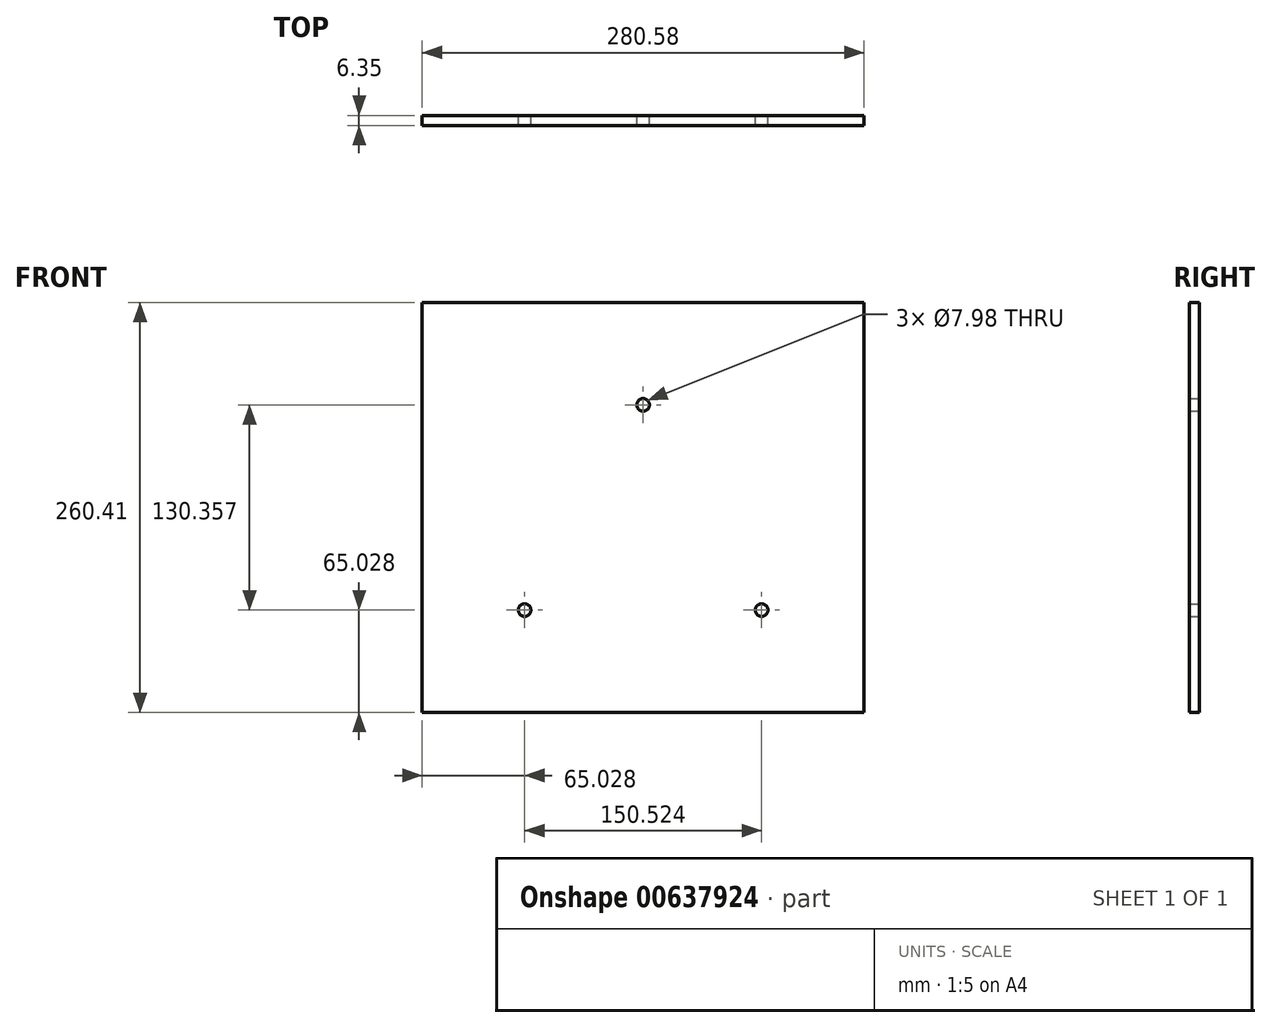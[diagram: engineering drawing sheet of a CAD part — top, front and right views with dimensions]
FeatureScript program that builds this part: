
annotation { "Feature Type Name" : "Feature", "Feature Type Description" : "" }
export const myFeature = defineFeature(function(context is Context, id is Id, definition is map)
    precondition{}
    {
        {
            var Q0;
            Q0=qCreatedBy(makeId("Front.planeOp"),FACE);
            var sketch = newSketch(context, id + "F0", { "sketchPlane" : qUnion([Q0])});
            skCircle(sketch, "E0.cCircle", {"center": v(0, 0) * mm, "radius": 102.65 * mm, "construction": true});
            skLineSegment(sketch, "E0.0", {"start": v(-82.08, -39.52) * mm, "end": v(-6.82, 90.84) * mm});
            skLineSegment(sketch, "E0.1", {"start": v(6.82, 90.84) * mm, "end": v(82.08, -39.52) * mm});
            skLineSegment(sketch, "E0.2", {"start": v(75.26, -51.33) * mm, "end": v(-75.26, -51.33) * mm});
            skPoint(sketch, "E1.visualSharp", {"position": v(0, 102.65) * mm});
            skArc(sketch, "E1.filletArc", {"start": v(6.82, 90.84) * mm, "mid": v(0, 94.78) * mm, "end": v(-6.82, 90.84) * mm});
            skPoint(sketch, "E2.visualSharp", {"position": v(-88.9, -51.33) * mm});
            skArc(sketch, "E2.filletArc", {"start": v(-82.08, -39.52) * mm, "mid": v(-82.08, -47.39) * mm, "end": v(-75.26, -51.33) * mm});
            skPoint(sketch, "E3.visualSharp", {"position": v(88.9, -51.33) * mm});
            skArc(sketch, "E3.filletArc", {"start": v(75.26, -51.33) * mm, "mid": v(82.08, -47.39) * mm, "end": v(82.08, -39.52) * mm});
            skCircle(sketch, "E4", {"center": v(0, 0) * mm, "radius": 86.9 * mm, "construction": true});
            skLineSegment(sketch, "E5", {"start": v(-75.26, -43.45) * mm, "end": v(0, 0) * mm, "construction": true});
            skLineSegment(sketch, "E6", {"start": v(75.26, -43.45) * mm, "end": v(0, 0) * mm, "construction": true});
            skLineSegment(sketch, "E7", {"start": v(0, 86.9) * mm, "end": v(0, 0) * mm, "construction": true});
            skLineSegment(sketch, "E8", {"start": v(0, 86.9) * mm, "end": v(0, 151.93) * mm, "construction": true});
            skPoint(sketch, "E8.endSnap0", {"position": v(0, 94.78) * mm});
            skLineSegment(sketch, "E9", {"start": v(0, -51.33) * mm, "end": v(0, -108.48) * mm, "construction": true});
            skLineSegment(sketch, "E10", {"start": v(-75.26, -43.45) * mm, "end": v(-140.29, -43.45) * mm, "construction": true});
            skLineSegment(sketch, "E11", {"start": v(75.26, -43.45) * mm, "end": v(140.29, -43.45) * mm, "construction": true});
            skLineSegment(sketch, "E12", {"start": v(-140.29, 151.93) * mm, "end": v(140.29, 151.93) * mm});
            skLineSegment(sketch, "E13", {"start": v(140.29, 151.93) * mm, "end": v(140.29, -108.48) * mm});
            skLineSegment(sketch, "E14", {"start": v(140.29, -108.48) * mm, "end": v(-140.29, -108.48) * mm});
            skLineSegment(sketch, "E15", {"start": v(-140.29, -108.48) * mm, "end": v(-140.29, 151.93) * mm});
            skLineSegment(sketch, "E16.0", {"start": v(-89.49, 101.13) * mm, "end": v(89.49, 101.13) * mm, "construction": true});
            skLineSegment(sketch, "E16.1", {"start": v(-89.49, -57.68) * mm, "end": v(-89.49, 101.13) * mm, "construction": true});
            skLineSegment(sketch, "E16.2", {"start": v(89.49, -57.68) * mm, "end": v(-89.49, -57.68) * mm, "construction": true});
            skLineSegment(sketch, "E16.3", {"start": v(89.49, 101.13) * mm, "end": v(89.49, -57.68) * mm, "construction": true});
            skLineSegment(sketch, "E17", {"start": v(-89.49, 101.13) * mm, "end": v(-140.29, 151.93) * mm, "construction": true});
            skLineSegment(sketch, "E18", {"start": v(89.49, 101.13) * mm, "end": v(140.29, 151.93) * mm, "construction": true});
            skLineSegment(sketch, "E19", {"start": v(89.49, -57.68) * mm, "end": v(140.29, -108.48) * mm, "construction": true});
            skLineSegment(sketch, "E20", {"start": v(-89.49, -57.68) * mm, "end": v(-140.29, -108.48) * mm, "construction": true});
            skSolve(sketch);
        }
        {
            var Q0;
            Q0 = qSketchRegion(id + "F0", true);
            var Q1;
            Q1=makeQuery(id+"F0.imprint","IMPRINT",FACE,{"disambiguationData":[TD([[makeQuery(id+"F0.imprint","IMPRINT",EDGE,{"derivedFrom":sQuery(id+"F0.wireOp",EDGE,"E0.0")}),-1.0]])]});
            extrude(context, id + "F1", {"entities" : qUnion([Q0, Q1]), "depth" : 6.35 * mm, "offsetDistance" : 25.4 * mm});
        }
        {
            var Q0;
            Q0=sQuery(id+"F0.wireOp",VERTEX,"E7.start");
            var Q1;
            Q1=sQuery(id+"F0.wireOp",VERTEX,"E5.start");
            var Q2;
            Q2=sQuery(id+"F0.wireOp",VERTEX,"E3.filletArc.center");
            var Q3;
            Q3=makeQuery(id+"F1.opExtrude","SWEPT_BODY",BODY,{"disambiguationData":[OSD([sQuery(id+"F0.wireOp",EDGE,"E12"),sQuery(id+"F0.wireOp",EDGE,"E13"),sQuery(id+"F0.wireOp",EDGE,"E14"),sQuery(id+"F0.wireOp",EDGE,"E15")])]});
            hole(context, id + "F2", {"style" : HoleStyle.SIMPLE, "endStyle" : HoleEndStyle.THROUGH, "oppositeDirection" : true, "holeDiameter" : 7.98 * mm, "majorDiameter" : 6.35 * mm, "isTappedThrough" : true, "tappedDepth" : 12.7 * mm, "tapClearance" : 3, "locations" : qUnion([Q0, Q1, Q2]), "scope" : qUnion([Q3])});
        }
    });
